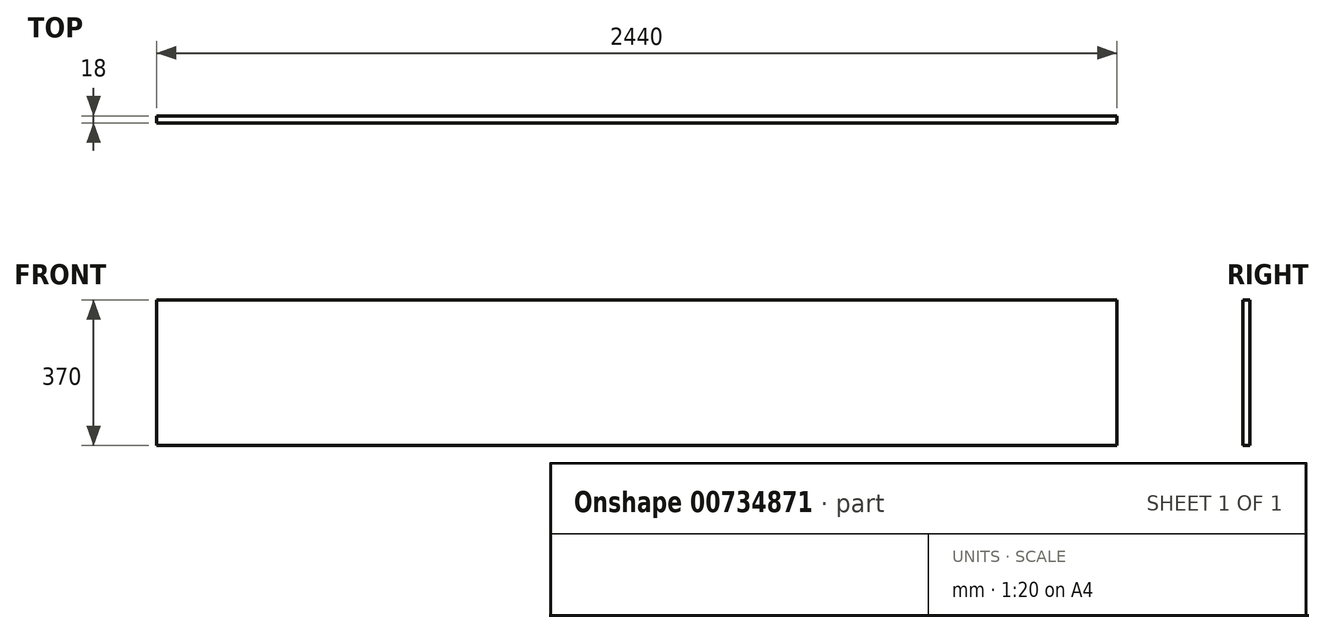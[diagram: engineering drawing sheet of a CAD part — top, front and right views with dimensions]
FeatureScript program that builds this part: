
annotation { "Feature Type Name" : "Feature", "Feature Type Description" : "" }
export const myFeature = defineFeature(function(context is Context, id is Id, definition is map)
    precondition{}
    {
        {
            var Q0;
            Q0=qCreatedBy(makeId("Front.planeOp"),FACE);
            var sketch = newSketch(context, id + "F0", { "sketchPlane" : qUnion([Q0])});
            skLineSegment(sketch, "E0.bottom", {"start": v(-1220, 185) * mm, "end": v(1220, 185) * mm});
            skLineSegment(sketch, "E0.top", {"start": v(-1220, -185) * mm, "end": v(1220, -185) * mm});
            skLineSegment(sketch, "E0.left", {"start": v(-1220, 185) * mm, "end": v(-1220, -185) * mm});
            skLineSegment(sketch, "E0.right", {"start": v(1220, 185) * mm, "end": v(1220, -185) * mm});
            skPoint(sketch, "E0.middle", {"position": v(0, 0) * mm});
            skSolve(sketch);
        }
        {
            var Q0;
            Q0=makeQuery(id+"F0.imprint","IMPRINT",FACE,{"disambiguationData":[TD([[makeQuery(id+"F0.imprint","IMPRINT",EDGE,{"derivedFrom":sQuery(id+"F0.wireOp",EDGE,"E0.bottom")}),-1.0]])]});
            extrude(context, id + "F1", {"entities" : qUnion([Q0]), "endBound" : BoundingType.SYMMETRIC, "depth" : 18 * mm, "offsetDistance" : 25.4 * mm});
        }
    });
